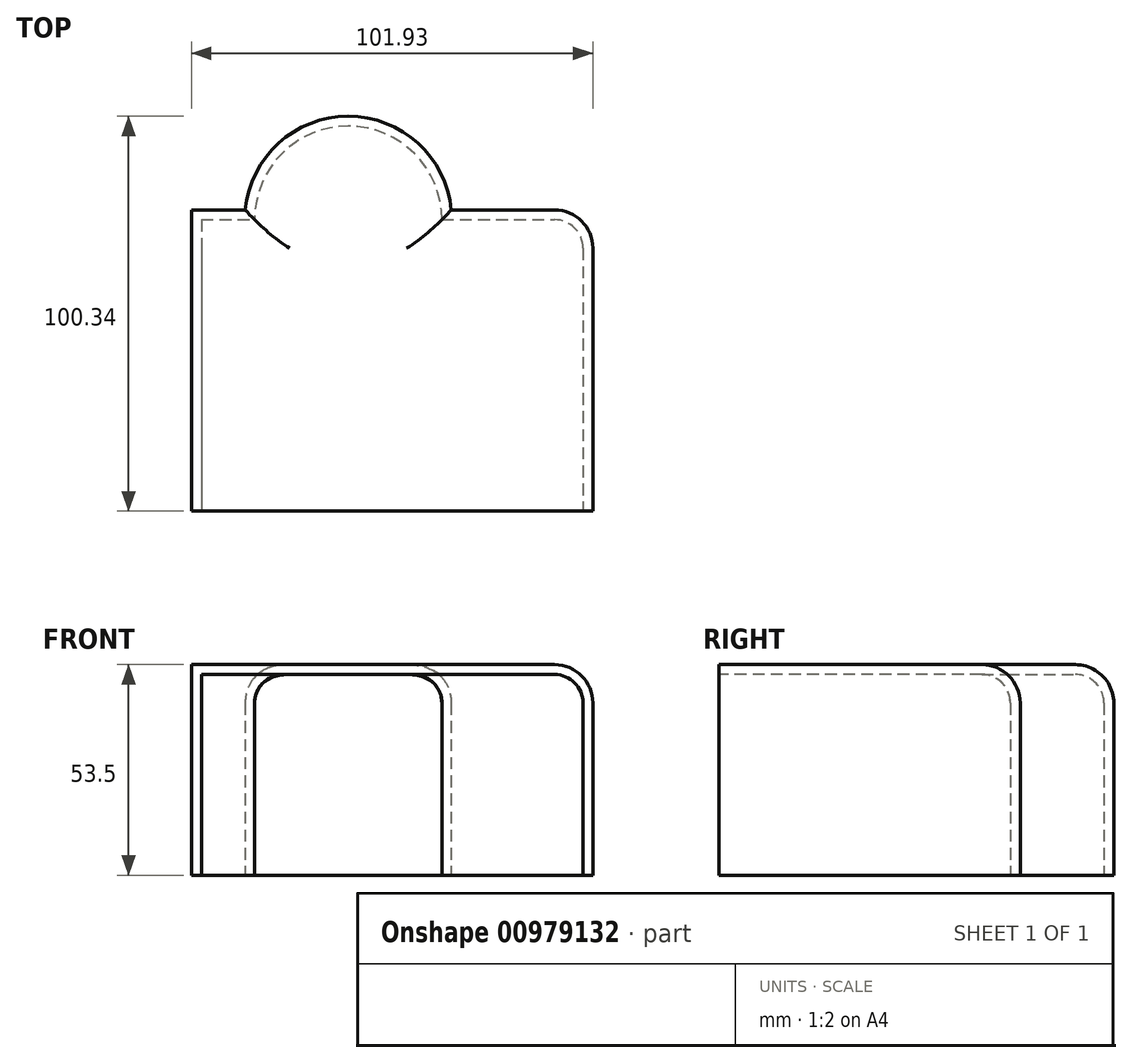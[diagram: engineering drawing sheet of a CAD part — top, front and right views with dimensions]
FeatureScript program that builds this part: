
annotation { "Feature Type Name" : "Feature", "Feature Type Description" : "" }
export const myFeature = defineFeature(function(context is Context, id is Id, definition is map)
    precondition{}
    {
        {
            var Q0;
            Q0=qCreatedBy(makeId("Top.planeOp"),FACE);
            var sketch = newSketch(context, id + "F0", { "sketchPlane" : qUnion([Q0])});
            skLineSegment(sketch, "E0.bottom", {"start": v(-79.65, 59.9) * mm, "end": v(17.28, 59.9) * mm});
            skLineSegment(sketch, "E0.top", {"start": v(-79.65, -14.15) * mm, "end": v(17.28, -14.15) * mm});
            skLineSegment(sketch, "E0.left", {"start": v(-79.65, 59.9) * mm, "end": v(-79.65, -14.15) * mm});
            skLineSegment(sketch, "E0.right", {"start": v(17.28, 59.9) * mm, "end": v(17.28, -14.15) * mm});
            skCircle(sketch, "E1", {"center": v(-42.38, 59.9) * mm, "radius": 23.79 * mm});
            skSolve(sketch);
        }
        {
            var Q0;
            Q0 = qSketchRegion(id + "F0", true);
            extrude(context, id + "F1", {"entities" : qUnion([Q0]), "depth" : 51 * mm, "offsetDistance" : 25 * mm});
        }
        {
            var Q0;
            Q0=makeQuery(id+"F1.opExtrude","SWEPT_EDGE",EDGE,{"disambiguationData":[OSD([sQuery(id+"F0.wireOp",EDGE,"E0.bottom"),sQuery(id+"F0.wireOp",EDGE,"E0.right")])]});
            var Q1;
            {var subQ0=sQuery(id+"F0.wireOp",EDGE,"E0.bottom");Q1=makeQuery(id+"F1.opExtrude","CAP_EDGE",EDGE,{"disambiguationData":[OSD([subQ0]),TDD([makeQuery(id+"F0.imprint","IMPRINT",EDGE,{"disambiguationData":[TD([[makeQuery(id+"F0.imprint","INTERSECT",VERTEX,{"derivedFrom":[subQ0,sQuery(id+"F0.wireOp",EDGE,"E0.right")]}),1.0]])],"derivedFrom":subQ0})])],"isStart":false});}
            var Q2;
            Q2=makeQuery(id+"F1.opExtrude","CAP_EDGE",EDGE,{"disambiguationData":[OSD([sQuery(id+"F0.wireOp",EDGE,"E0.right")])],"isStart":false});
            var Q3;
            Q3=makeQuery(id+"F1.opExtrude","CAP_EDGE",EDGE,{"disambiguationData":[OSD([sQuery(id+"F0.wireOp",EDGE,"E1")])],"isStart":false});
            var Q4;
            {var subQ0=sQuery(id+"F0.wireOp",EDGE,"E0.bottom");Q4=makeQuery(id+"F1.opExtrude","CAP_EDGE",EDGE,{"disambiguationData":[OSD([subQ0]),TDD([makeQuery(id+"F0.imprint","IMPRINT",EDGE,{"disambiguationData":[TD([[makeQuery(id+"F0.imprint","INTERSECT",VERTEX,{"derivedFrom":[subQ0,sQuery(id+"F0.wireOp",EDGE,"E0.left")]}),-1.0]])],"derivedFrom":subQ0})])],"isStart":false});}
            fillet(context, id + "F2", {"entities" : qUnion([Q0, Q1, Q2, Q3, Q4]), "radius" : 7.24 * mm, "tangentPropagation" : true, "allowEdgeOverflow" : false});
        }
        {
            var Q0;
            Q0=makeQuery(id+"F1.opExtrude","SWEPT_FACE",FACE,{"disambiguationData":[OSD([sQuery(id+"F0.wireOp",EDGE,"E0.top")])]});
            var Q1;
            Q1=makeQuery(id+"F1.opExtrude","CAP_FACE",FACE,{"disambiguationData":[OSD([sQuery(id+"F0.wireOp",EDGE,"E0.bottom"),sQuery(id+"F0.wireOp",EDGE,"E0.top"),sQuery(id+"F0.wireOp",EDGE,"E0.left"),sQuery(id+"F0.wireOp",EDGE,"E0.right"),sQuery(id+"F0.wireOp",EDGE,"E1")])],"isStart":true});
            shell(context, id + "F3", {"entities" : qUnion([Q0, Q1]), "thickness" : 2.5 * mm, "oppositeDirection" : true});
        }
    });
